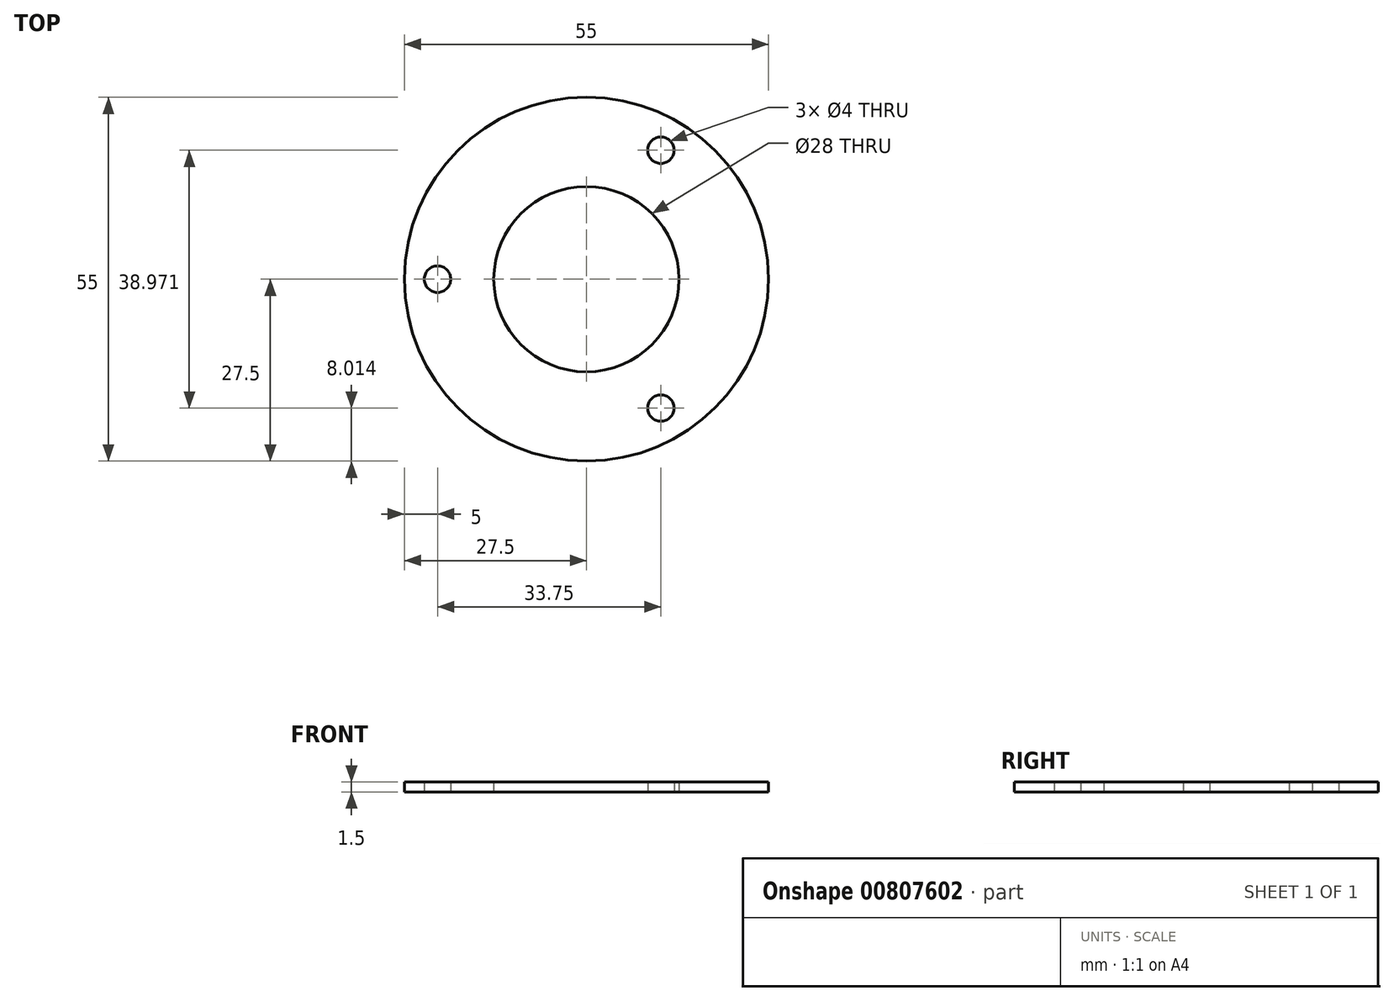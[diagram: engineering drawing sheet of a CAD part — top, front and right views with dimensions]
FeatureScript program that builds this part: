
annotation { "Feature Type Name" : "Feature", "Feature Type Description" : "" }
export const myFeature = defineFeature(function(context is Context, id is Id, definition is map)
    precondition{}
    {
        {
            var Q0;
            Q0=qCreatedBy(makeId("Top.planeOp"),FACE);
            var sketch = newSketch(context, id + "F0", { "sketchPlane" : qUnion([Q0])});
            skCircle(sketch, "E0", {"center": v(0, 0) * mm, "radius": 27.5 * mm});
            skCircle(sketch, "E1", {"center": v(0, 0) * mm, "radius": 14 * mm});
            skCircle(sketch, "E2", {"center": v(0, 0) * mm, "radius": 22.5 * mm, "construction": true});
            skLineSegment(sketch, "E3", {"start": v(0, 0) * mm, "end": v(-31.01, 0) * mm});
            skCircle(sketch, "E4", {"center": v(-22.5, 0) * mm, "radius": 2 * mm});
            skCircle(sketch, "E5.1.0", {"center": v(11.25, -19.49) * mm, "radius": 2 * mm});
            skCircle(sketch, "E5.2.0", {"center": v(11.25, 19.49) * mm, "radius": 2 * mm});
            skSolve(sketch);
        }
        {
            var Q0;
            Q0 = qSketchRegion(id + "F0", true);
            extrude(context, id + "F1", {"entities" : qUnion([Q0]), "depth" : 1.5 * mm, "offsetDistance" : 25 * mm});
        }
    });
